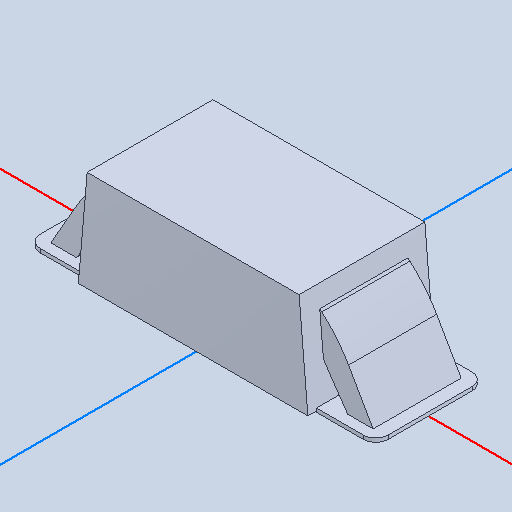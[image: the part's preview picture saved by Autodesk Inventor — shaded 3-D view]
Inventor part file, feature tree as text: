
AUTODESK INVENTOR PART (.ipt)
format: ipt  version: 2022 (Build 260153000, 153)  size: 113,664 bytes
history: native  units: mm
features: other x3, chamfer x1, boolean_combine x1, mirror x1
ambient origin geometry x8: Origin, YZ Plane, XZ Plane, XY Plane, X Axis, Y Axis, Z Axis, Center Point
bodies: Body1 (feature_tree), Body2 (feature_tree), Body3 (feature_tree)
feature tree (6):
  other  "Твердое тело1"
  other  "Твердое тело2"
  other  "Твердое тело3"
  chamfer  "Chamfer1"  [1 undecoded]
  boolean_combine  "Combine1"
  mirror  "Mirror2"
note: 1 required parameter value undecoded (feature->parameter linkage not recoverable at this tier; creation-order binding heuristic only, values carry confidence <= 0.55)
